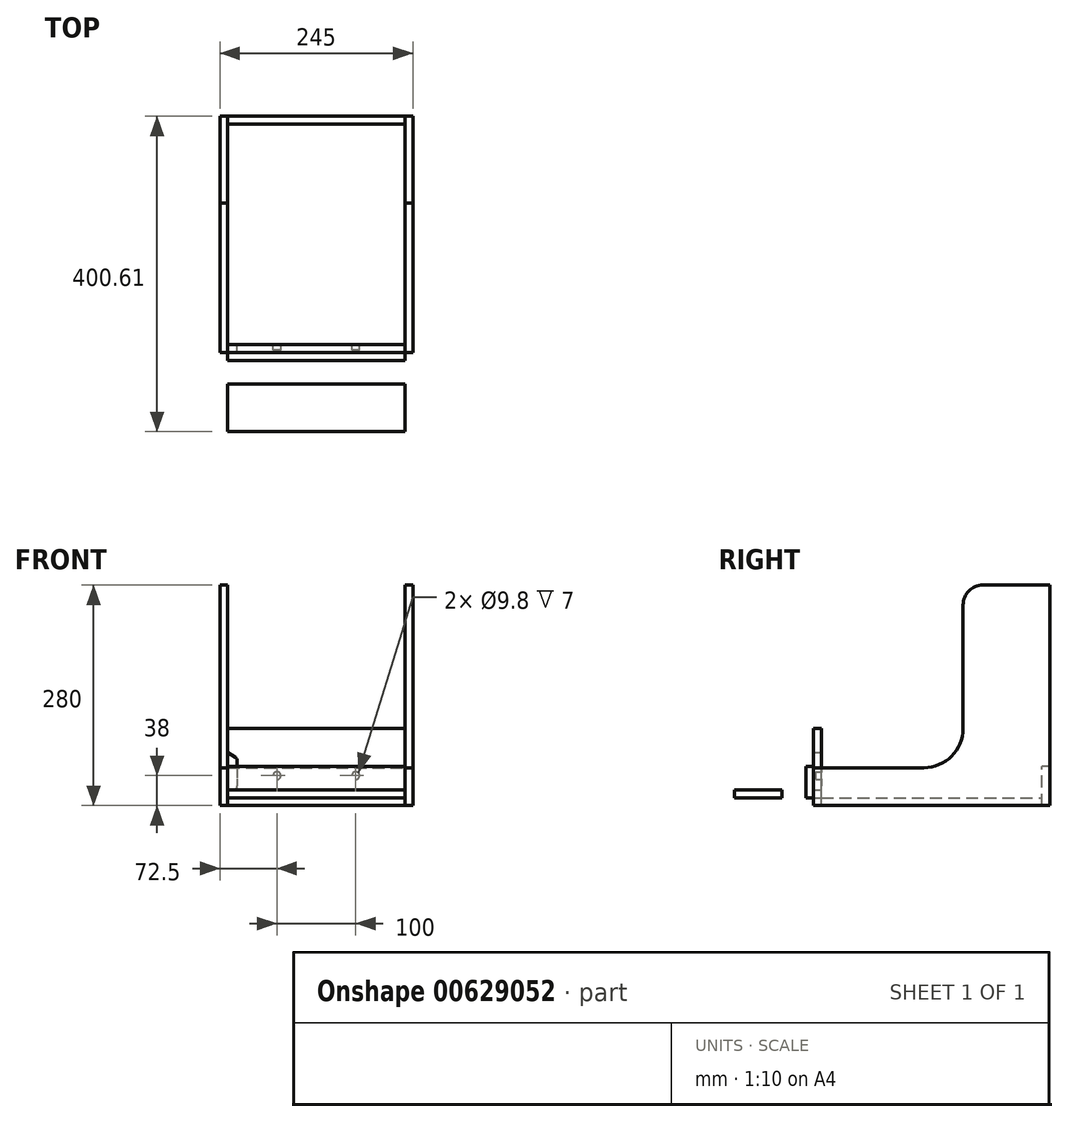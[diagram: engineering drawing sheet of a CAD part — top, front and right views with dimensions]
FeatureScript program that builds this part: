
annotation { "Feature Type Name" : "Feature", "Feature Type Description" : "" }
export const myFeature = defineFeature(function(context is Context, id is Id, definition is map)
    precondition{}
    {
        {
            var Q0;
            Q0=qCreatedBy(makeId("Top.planeOp"),FACE);
            var sketch = newSketch(context, id + "F0", { "sketchPlane" : qUnion([Q0])});
            skLineSegment(sketch, "E0.bottom", {"start": v(0, 0) * mm, "end": v(225, 0) * mm});
            skLineSegment(sketch, "E0.top", {"start": v(0, 280) * mm, "end": v(225, 280) * mm});
            skLineSegment(sketch, "E0.left", {"start": v(0, 0) * mm, "end": v(0, 280) * mm});
            skLineSegment(sketch, "E0.right", {"start": v(225, 0) * mm, "end": v(225, 280) * mm});
            skSolve(sketch);
        }
        {
            var Q0;
            Q0=qSketchRegion(id+"F0",true);
            extrude(context, id + "F1", {"entities" : qUnion([Q0]), "oppositeDirection" : true, "depth" : 10 * mm, "offsetDistance" : 25 * mm});
        }
        {
            var Q0;
            Q0=makeQuery(id+"F1.opExtrude","SWEPT_FACE",FACE,{"disambiguationData":[OSD([sQuery(id+"F0.wireOp",EDGE,"E0.bottom")])]});
            var sketch = newSketch(context, id + "F2", { "sketchPlane" : qUnion([Q0])});
            skLineSegment(sketch, "E1.bottom", {"start": v(0, -10) * mm, "end": v(225, -10) * mm});
            skLineSegment(sketch, "E1.top", {"start": v(0, 38) * mm, "end": v(225, 38) * mm});
            skLineSegment(sketch, "E1.left", {"start": v(0, -10) * mm, "end": v(0, 38) * mm});
            skLineSegment(sketch, "E1.right", {"start": v(225, -10) * mm, "end": v(225, 38) * mm});
            skLineSegment(sketch, "E2", {"start": v(112.5, 115.53) * mm, "end": v(112.5, -106.42) * mm, "construction": true});
            skPoint(sketch, "E2.startSnap0", {"position": v(112.5, 38) * mm});
            skPoint(sketch, "E2.endSnap0", {"position": v(112.5, -10) * mm});
            skCircle(sketch, "E3", {"center": v(62.5, 28) * mm, "radius": 4.9 * mm});
            skLineSegment(sketch, "E4", {"start": v(-46.24, 28) * mm, "end": v(234.78, 28) * mm, "construction": true});
            skCircle(sketch, "E5", {"center": v(162.5, 28) * mm, "radius": 4.9 * mm});
            skSolve(sketch);
        }
        {
            var Q0;
            Q0=qSketchRegion(id+"F2",true);
            var Q1;
            Q1=makeQuery(id+"F2.imprint","IMPRINT",FACE,{"disambiguationData":[TD([[makeQuery(id+"F2.imprint","IMPRINT",EDGE,{"derivedFrom":sQuery(id+"F2.wireOp",EDGE,"E3")}),1.0]])]});
            var Q2;
            Q2=makeQuery(id+"F2.imprint","IMPRINT",FACE,{"disambiguationData":[TD([[makeQuery(id+"F2.imprint","IMPRINT",EDGE,{"derivedFrom":sQuery(id+"F2.wireOp",EDGE,"E5")}),1.0]])]});
            extrude(context, id + "F3", {"entities" : qUnion([Q0, Q1, Q2]), "depth" : 10 * mm, "offsetDistance" : 25 * mm});
        }
        {
            var Q0;
            Q0=makeQuery(id+"F2.imprint","IMPRINT",FACE,{"disambiguationData":[TD([[makeQuery(id+"F2.imprint","IMPRINT",EDGE,{"derivedFrom":sQuery(id+"F2.wireOp",EDGE,"E3")}),1.0]])]});
            var Q1;
            Q1=makeQuery(id+"F2.imprint","IMPRINT",FACE,{"disambiguationData":[TD([[makeQuery(id+"F2.imprint","IMPRINT",EDGE,{"derivedFrom":sQuery(id+"F2.wireOp",EDGE,"E5")}),1.0]])]});
            extrude(context, id + "F4", {"entities" : qUnion([Q0, Q1]), "operationType" : NewBodyOperationType.REMOVE, "depth" : 7 * mm, "offsetDistance" : 25 * mm});
        }
        {
            var Q0;
            Q0=makeQuery(id+"F1.opExtrude","SWEPT_FACE",FACE,{"disambiguationData":[OSD([sQuery(id+"F0.wireOp",EDGE,"E0.top")])]});
            var sketch = newSketch(context, id + "F5", { "sketchPlane" : qUnion([Q0])});
            skPoint(sketch, "E6.oppositeSnap0", {"position": v(0, -5) * mm});
            skLineSegment(sketch, "E6.bottom", {"start": v(-225, -10) * mm, "end": v(0, -10) * mm});
            skLineSegment(sketch, "E6.top", {"start": v(-225, 40) * mm, "end": v(0, 40) * mm});
            skLineSegment(sketch, "E6.left", {"start": v(-225, -10) * mm, "end": v(-225, 40) * mm});
            skLineSegment(sketch, "E6.right", {"start": v(0, -10) * mm, "end": v(0, 40) * mm});
            skSolve(sketch);
        }
        {
            var Q0;
            Q0=qSketchRegion(id+"F5",true);
            extrude(context, id + "F6", {"entities" : qUnion([Q0]), "depth" : 10 * mm, "offsetDistance" : 25 * mm});
        }
        {
            var Q0;
            Q0=makeQuery(id+"F1.opExtrude","SWEPT_FACE",FACE,{"disambiguationData":[OSD([sQuery(id+"F0.wireOp",EDGE,"E0.right")])]});
            var sketch = newSketch(context, id + "F7", { "sketchPlane" : qUnion([Q0])});
            skLineSegment(sketch, "E7.top", {"start": v(290, 270) * mm, "end": v(205, 270) * mm});
            skLineSegment(sketch, "E7.right", {"start": v(180, 88) * mm, "end": v(180, 245) * mm});
            skLineSegment(sketch, "E8.0", {"start": v(-10, -10) * mm, "end": v(-10, 38) * mm});
            skLineSegment(sketch, "E9", {"start": v(-10, 38) * mm, "end": v(130, 38) * mm});
            skLineSegment(sketch, "E10", {"start": v(-10, -10) * mm, "end": v(290, -10) * mm});
            skLineSegment(sketch, "E11", {"start": v(290, -10) * mm, "end": v(290, 270) * mm});
            skPoint(sketch, "E12.visualSharp", {"position": v(180, 38) * mm});
            skArc(sketch, "E12.filletArc", {"start": v(130, 38) * mm, "mid": v(165.36, 52.64) * mm, "end": v(180, 88) * mm});
            skPoint(sketch, "E13.visualSharp", {"position": v(180, 270) * mm});
            skArc(sketch, "E13.filletArc", {"start": v(205, 270) * mm, "mid": v(187.32, 262.68) * mm, "end": v(180, 245) * mm});
            skSolve(sketch);
        }
        {
            var Q0;
            Q0=makeQuery(id+"F1.opExtrude","SWEPT_FACE",FACE,{"disambiguationData":[OSD([sQuery(id+"F0.wireOp",EDGE,"E0.left")])]});
            var sketch = newSketch(context, id + "F8", { "sketchPlane" : qUnion([Q0])});
            skLineSegment(sketch, "E14.0", {"start": v(10, -10) * mm, "end": v(10, 38) * mm});
            skLineSegment(sketch, "E15", {"start": v(10, 38) * mm, "end": v(-130, 38) * mm});
            skLineSegment(sketch, "E16", {"start": v(-205, 270) * mm, "end": v(-290, 270) * mm});
            skLineSegment(sketch, "E17", {"start": v(-180, 245) * mm, "end": v(-180, 88) * mm});
            skPoint(sketch, "E18", {"position": v(-235, 270) * mm});
            skLineSegment(sketch, "E19", {"start": v(10, -10) * mm, "end": v(-290, -10) * mm});
            skLineSegment(sketch, "E20", {"start": v(-290, -10) * mm, "end": v(-290, 270) * mm});
            skPoint(sketch, "E21.visualSharp", {"position": v(-180, 38) * mm});
            skArc(sketch, "E21.filletArc", {"start": v(-180, 88) * mm, "mid": v(-165.36, 52.64) * mm, "end": v(-130, 38) * mm});
            skPoint(sketch, "E22.visualSharp", {"position": v(-180, 270) * mm});
            skArc(sketch, "E22.filletArc", {"start": v(-180, 245) * mm, "mid": v(-187.32, 262.68) * mm, "end": v(-205, 270) * mm});
            skSolve(sketch);
        }
        {
            var Q0;
            Q0=makeQuery(id+"F3.opExtrude","CAP_FACE",FACE,{"disambiguationData":[OSD([sQuery(id+"F2.wireOp",EDGE,"E1.bottom"),sQuery(id+"F2.wireOp",EDGE,"E1.top"),sQuery(id+"F2.wireOp",EDGE,"E1.left"),sQuery(id+"F2.wireOp",EDGE,"E1.right")])],"isStart":false});
            var sketch = newSketch(context, id + "F9", { "sketchPlane" : qUnion([Q0])});
            skLineSegment(sketch, "E23.0", {"start": v(0, 0) * mm, "end": v(225, 0) * mm});
            skLineSegment(sketch, "E24.bottom", {"start": v(0, 0) * mm, "end": v(220, 0) * mm});
            skLineSegment(sketch, "E25.top", {"start": v(0, 40) * mm, "end": v(225, 40) * mm});
            skLineSegment(sketch, "E25.left", {"start": v(0, 0) * mm, "end": v(0, 40) * mm});
            skLineSegment(sketch, "E25.right", {"start": v(225, 0) * mm, "end": v(225, 40) * mm});
            skSolve(sketch);
        }
        {
            var Q0;
            {var subQ1=sQuery(id+"F0.wireOp",EDGE,"E0.left");var subQ2=makeQuery(id+"F1.opExtrude","SWEPT_EDGE",EDGE,{"disambiguationData":[OSD([sQuery(id+"F0.wireOp",EDGE,"E0.bottom"),subQ1])]});Q0=makeQuery(id+"F8.imprint","IMPRINT",FACE,{"disambiguationData":[TD([[makeQuery(id+"F8.imprint","IMPRINT",EDGE,{"derivedFrom":subQ2}),1.0]])]});}
            var Q1;
            {var subQ6=sQuery(id+"F8.wireOp",EDGE,"E14.0");Q1=makeQuery(id+"F8.imprint","IMPRINT",FACE,{"disambiguationData":[TD([[makeQuery(id+"F8.imprint","IMPRINT",EDGE,{"derivedFrom":subQ6}),1.0]])]});}
            extrude(context, id + "F10", {"entities" : qUnion([Q0, Q1]), "depth" : 10 * mm, "offsetDistance" : 25 * mm});
        }
        {
            var Q0;
            Q0=makeQuery(id+"F7.imprint","IMPRINT",FACE,{"disambiguationData":[TD([[makeQuery(id+"F7.imprint","IMPRINT",EDGE,{"derivedFrom":sQuery(id+"F7.wireOp",EDGE,"E7.top")}),1.0]])]});
            var Q1;
            {var subQ1=sQuery(id+"F0.wireOp",EDGE,"E0.right");Q1=makeQuery(id+"F7.imprint","IMPRINT",FACE,{"disambiguationData":[TD([[makeQuery(id+"F7.imprint","IMPRINT",EDGE,{"derivedFrom":makeQuery(id+"F1.opExtrude","CAP_EDGE",EDGE,{"disambiguationData":[OSD([subQ1])],"isStart":true})}),-1.0]])]});}
            extrude(context, id + "F11", {"entities" : qUnion([Q0, Q1]), "depth" : 10 * mm, "offsetDistance" : 25 * mm});
        }
        {
            var Q0;
            Q0=qSketchRegion(id+"F9",true);
            extrude(context, id + "F12", {"entities" : qUnion([Q0]), "depth" : 10 * mm, "offsetDistance" : 25 * mm});
        }
        {
            var Q0;
            Q0=qCreatedBy(makeId("Front.planeOp"),FACE);
            var sketch = newSketch(context, id + "F13", { "sketchPlane" : qUnion([Q0])});
            skLineSegment(sketch, "E26.bottom", {"start": v(0, 0) * mm, "end": v(225, 0) * mm});
            skLineSegment(sketch, "E26.top", {"start": v(0, 88) * mm, "end": v(225, 88) * mm});
            skLineSegment(sketch, "E26.left", {"start": v(0, 0) * mm, "end": v(0, 88) * mm});
            skLineSegment(sketch, "E26.right", {"start": v(225, 0) * mm, "end": v(225, 88) * mm});
            skLineSegment(sketch, "E27", {"start": v(0, 57.5) * mm, "end": v(9.78, 50.97) * mm});
            skLineSegment(sketch, "E28", {"start": v(12, 46.82) * mm, "end": v(12, 15) * mm});
            skLineSegment(sketch, "E29", {"start": v(7, 10) * mm, "end": v(0, 10) * mm});
            skPoint(sketch, "E30.visualSharp", {"position": v(12, 10) * mm});
            skArc(sketch, "E30.filletArc", {"start": v(7, 10) * mm, "mid": v(10.54, 11.46) * mm, "end": v(12, 15) * mm});
            skPoint(sketch, "E31.visualSharp", {"position": v(12, 49.49) * mm});
            skArc(sketch, "E31.filletArc", {"start": v(12, 46.82) * mm, "mid": v(11.4, 49.17) * mm, "end": v(9.78, 50.97) * mm});
            skSolve(sketch);
        }
        {
            var Q0;
            {var subQ3=sQuery(id+"F13.wireOp",EDGE,"E26.bottom");Q0=makeQuery(id+"F13.imprint","IMPRINT",FACE,{"disambiguationData":[TD([[makeQuery(id+"F13.imprint","IMPRINT",EDGE,{"derivedFrom":subQ3}),1.0]])]});}
            extrude(context, id + "F14", {"entities" : qUnion([Q0]), "depth" : 10 * mm, "offsetDistance" : 25 * mm});
        }
        {
            var Q0;
            Q0=qCreatedBy(makeId("Top.planeOp"),FACE);
            var sketch = newSketch(context, id + "F15", { "sketchPlane" : qUnion([Q0])});
            skLineSegment(sketch, "E32.bottom", {"start": v(0, -50.1) * mm, "end": v(225, -50.1) * mm});
            skLineSegment(sketch, "E32.top", {"start": v(0, -110.6) * mm, "end": v(225, -110.6) * mm});
            skLineSegment(sketch, "E32.left", {"start": v(0, -50.1) * mm, "end": v(0, -110.6) * mm});
            skLineSegment(sketch, "E32.right", {"start": v(225, -50.1) * mm, "end": v(225, -110.6) * mm});
            skSolve(sketch);
        }
        {
            var Q0;
            Q0 = qSketchRegion(id + "F15", true);
            extrude(context, id + "F16", {"entities" : qUnion([Q0]), "depth" : 10 * mm, "offsetDistance" : 25 * mm});
        }
    });
